# Revit family: EKF_EE_ПластронСВырезомTrivia_AVERES
name_source: partatom
category: Электрооборудование
units: mm (PartAtom-declared; Revit-internal decimal feet)

## family parameters
Всегда вертикально = Нет
На основе рабочей плоскости = Да
Общий = Да
При загрузке вырезать с полостями = Нет
Размер круглого соединителя = Использовать диаметр
Тип детали = Силовой щит
Точка расчета площади = Нет

## types (36) — shared parameters
ADSK_Единица измерения = шт.
ADSK_Завод-изготовитель = EKF
ADSK_Количество = 1
ADSK_Материал = RAL 7035_Сталь
Глубина = 400 мм
Изготовитель = EKF
Отметка по умолчанию = 1219.2 мм
Серия номенклатуры = Averes
Степень защиты IP = -
ТВ = EKF_2_TRIVIA_AVERES
Тип установки = -
Шаг_НабораПластронов_2шт = 100 мм
zero-valued in all types: ADSK_Масса

## per-type parameters (varying)
| type | ADSK_Код изделия | ADSK_Марка | ADSK_Наименование | ADSK_Обозначение | ADSK_Размер_Высота | ADSK_Размер_Глубина | ADSK_Размер_Ширина | Тип | Тип_Пластрона |
| Пластрон в вырезом  для горизонтального  ВА-99/160 3Р | FPFU2204 | Пластрон в вырезом для горизонтального ВА-99/160 3Р | Пластрон в вырезом для горизонтального ВА-99/160 3Р | Пластрон в вырезом для горизонтального ВА-99/160 3Р | 198 мм | 14 мм | 490 мм | 564 мм | Вл_Пластрон1 |
| Пластрон с вырезом  для горизонтального  AV POWER-1  ТМ 3P/4P с моторным приводом | FPFU1104 | Пластрон с вырезом для горизонтального AV POWER-1 ТМ 3P/4P с моторным приводом | Пластрон с вырезом для горизонтального AV POWER-1 ТМ 3P/4P с моторным приводом | Пластрон с вырезом для горизонтального AV POWER-1 ТМ 3P/4P с моторным приводом | 148 мм | 15 мм | 490 мм | 608 мм | Вл_Пластрон4 |
| Пластрон с вырезом для 1-го вертикального AV POWER-4 TM/ETU 3P EKF AVERES | FPFU1004 | Пластрон с вырезом для 1-го вертикального AV POWER-4 TM/ETU 3P EKF AVERES | Пластрон с вырезом для 1-го вертикального AV POWER-4 TM/ETU 3P EKF AVERES | Пластрон с вырезом для 1-го вертикального AV POWER-4 TM/ETU 3P EKF AVERES | 398 мм | 15 мм | 490 мм | 609 мм | Вл_Пластрон4 |
| Пластрон с вырезом для 3-х вертикальных AV POWER-3 TM/ETU 3P EKF AVERES | FPFU0904 | Пластрон с вырезом для 3-х вертикальных AV POWER-3 TM/ETU 3P EKF AVERES | Пластрон с вырезом для 3-х вертикальных AV POWER-3 TM/ETU 3P EKF AVERES | Пластрон с вырезом для 3-х вертикальных AV POWER-3 TM/ETU 3P EKF AVERES | 378 мм | 15 мм | 490 мм | 610 мм | Вл_Пластрон4 |
| Пластрон с вырезом для 4-х вертикальных AV POWER-1 ETU 3P EKF AVERES | FPFU0704 | Пластрон с вырезом для 4-х вертикальных AV POWER-1 ETU 3P EKF AVERES | Пластрон с вырезом для 4-х вертикальных AV POWER-1 ETU 3P EKF AVERES | Пластрон с вырезом для 4-х вертикальных AV POWER-1 ETU 3P EKF AVERES | 248 мм | 15 мм | 490 мм | 611 мм | Вл_Пластрон4 |
| Пластрон с вырезом для 4-х вертикальных AV POWER-1 TM 3P EKF AVERES | FPFU0604 | Пластрон с вырезом для 4-х вертикальных AV POWER-1 TM 3P EKF AVERES | Пластрон с вырезом для 4-х вертикальных AV POWER-1 TM 3P EKF AVERES | Пластрон с вырезом для 4-х вертикальных AV POWER-1 TM 3P EKF AVERES | 198 мм | 15 мм | 490 мм | 612 мм | Вл_Пластрон4 |
| Пластрон с вырезом для 4-х вертикальных AV POWER-2 TM/ETU 3P EKF AVERES | FPFU0804 | Пластрон с вырезом для 4-х вертикальных AV POWER-2 TM/ETU 3P EKF AVERES | Пластрон с вырезом для 4-х вертикальных AV POWER-2 TM/ETU 3P EKF AVERES | Пластрон с вырезом для 4-х вертикальных AV POWER-2 TM/ETU 3P EKF AVERES | 248 мм | 15 мм | 490 мм | 613 мм | Вл_Пластрон4 |
| Пластрон с вырезом для вертикальных ВА-99/125 4х3Р/3х4Р EKF AVERES | FPFU3104 | Пластрон с вырезом для вертикальных ВА-99/125 4х3Р/3х4Р EKF AVERES | Пластрон с вырезом для вертикальных ВА-99/125 4х3Р/3х4Р EKF AVERES | Пластрон с вырезом для вертикальных ВА-99/125 4х3Р/3х4Р EKF AVERES | 248 мм | 15 мм | 490 мм | 615 мм | Вл_Пластрон4 |
| Пластрон с вырезом для вертикальных ВА-99/250 3х3Р/3х4Р EKF AVERES | FPFU3304 | Пластрон с вырезом для вертикальных ВА-99/250 3х3Р/3х4Р EKF AVERES | Пластрон с вырезом для вертикальных ВА-99/250 3х3Р/3х4Р EKF AVERES | Пластрон с вырезом для вертикальных ВА-99/250 3х3Р/3х4Р EKF AVERES | 248 мм | 15 мм | 490 мм | 616 мм | Вл_Пластрон4 |
| Пластрон с вырезом для вертикальных ВА-99/400 3х3Р/2х4Р EKF AVERES | FPFU3404 | Пластрон с вырезом для вертикальных ВА-99/400 3х3Р/2х4Р EKF AVERES | Пластрон с вырезом для вертикальных ВА-99/400 3х3Р/2х4Р EKF AVERES | Пластрон с вырезом для вертикальных ВА-99/400 3х3Р/2х4Р EKF AVERES | 348 мм | 15 мм | 490 мм | 617 мм | Вл_Пластрон4 |
| Пластрон с вырезом для вертикальных ВА-99С/100/160/250 3х3Р EKF AVERES | FPFU6604 | Пластрон с вырезом для вертикальных ВА-99С/100/160/250 3х3Р EKF AVERES | Пластрон с вырезом для вертикальных ВА-99С/100/160/250 3х3Р EKF AVERES | Пластрон с вырезом для вертикальных ВА-99С/100/160/250 3х3Р EKF AVERES | 248 мм | 15 мм | 490 мм | 618 мм | Вл_Пластрон4 |
| Пластрон с вырезом для вертикальных ВА-99С/400/630 3х3Р/2х4Р EKF AVERES | FPFU6704 | Пластрон с вырезом для вертикальных ВА-99С/400/630 3х3Р/2х4Р EKF AVERES | Пластрон с вырезом для вертикальных ВА-99С/400/630 3х3Р/2х4Р EKF AVERES | Пластрон с вырезом для вертикальных ВА-99С/400/630 3х3Р/2х4Р EKF AVERES | 348 мм | 15 мм | 490 мм | 619 мм | Вл_Пластрон4 |
| Пластрон с вырезом для выкатного ВА-45/2000 3Р/4Р EKF AVERES | FPFU4404 | Пластрон с вырезом для выкатного ВА-45/2000 3Р/4Р EKF AVERES | Пластрон с вырезом для выкатного ВА-45/2000 3Р/4Р EKF AVERES | Пластрон с вырезом для выкатного ВА-45/2000 3Р/4Р EKF AVERES | 548 мм | 15 мм | 490 мм | 620 мм | Вл_Пластрон4 |
| Пластрон с вырезом для выкатного ВА-45/3200 3Р/4Р EKF AVERES | FPFU4504 | Пластрон с вырезом для выкатного ВА-45/3200 3Р/4Р EKF AVERES | Пластрон с вырезом для выкатного ВА-45/3200 3Р/4Р EKF AVERES | Пластрон с вырезом для выкатного ВА-45/3200 3Р/4Р EKF AVERES | 548 мм | 15 мм | 490 мм | 621 мм | Вл_Пластрон4 |
| Пластрон с вырезом для выкатного ВА-45/4000 3Р/4Р EKF AVERES | FPFU4604 | Пластрон с вырезом для выкатного ВА-45/4000 3Р/4Р EKF AVERES | Пластрон с вырезом для выкатного ВА-45/4000 3Р/4Р EKF AVERES | Пластрон с вырезом для выкатного ВА-45/4000 3Р/4Р EKF AVERES | 548 мм | 15 мм | 490 мм | 622 мм | Вл_Пластрон4 |
| Пластрон с вырезом для выкатного ВА-450 3Р/4Р EKF AVERES | FPFU4804 | Пластрон с вырезом для выкатного ВА-450 3Р/4Р EKF AVERES | Пластрон с вырезом для выкатного ВА-450 3Р/4Р EKF AVERES | Пластрон с вырезом для выкатного ВА-450 3Р/4Р EKF AVERES | 498 мм | 15 мм | 690 мм | 623 мм | Вл_Пластрон4 |
| Пластрон с вырезом для горизонтального AV POWER-1 ETU 3P EKF AVERES | FPFU0204 | Пластрон с вырезом для горизонтального AV POWER-1 ETU 3P EKF AVERES | Пластрон с вырезом для горизонтального AV POWER-1 ETU 3P EKF AVERES | Пластрон с вырезом для горизонтального AV POWER-1 ETU 3P EKF AVERES | 198 мм | 15 мм | 490 мм | 625 мм | Вл_Пластрон4 |
| Пластрон с вырезом для горизонтального AV POWER-1 TM 3P EKF AVERES | FPFU0104 | Пластрон с вырезом для горизонтального AV POWER-1 TM 3P EKF AVERES | Пластрон с вырезом для горизонтального AV POWER-1 TM 3P EKF AVERES | Пластрон с вырезом для горизонтального AV POWER-1 TM 3P EKF AVERES | 148 мм | 15 мм | 490 мм | 626 мм | Вл_Пластрон4 |
| Пластрон с вырезом для горизонтального AV POWER-2 TM/ETU 3P EKF AVERES | FPFU0304 | Пластрон с вырезом для горизонтального AV POWER-2 TM/ETU 3P EKF AVERES | Пластрон с вырезом для горизонтального AV POWER-2 TM/ETU 3P EKF AVERES | Пластрон с вырезом для горизонтального AV POWER-2 TM/ETU 3P EKF AVERES | 198 мм | 15 мм | 490 мм | 627 мм | Вл_Пластрон4 |
| Пластрон с вырезом для горизонтального AV POWER-3 TM/ETU 3P EKF AVERES | FPFU0404 | Пластрон с вырезом для горизонтального AV POWER-3 TM/ETU 3P EKF AVERES | Пластрон с вырезом для горизонтального AV POWER-3 TM/ETU 3P EKF AVERES | Пластрон с вырезом для горизонтального AV POWER-3 TM/ETU 3P EKF AVERES | 248 мм | 15 мм | 490 мм | 628 мм | Вл_Пластрон4 |
| Пластрон с вырезом для горизонтального AV POWER-4 TM/ETU 3P EKF AVERES | FPFU0504 | Пластрон с вырезом для горизонтального AV POWER-4 TM/ETU 3P EKF AVERES | Пластрон с вырезом для горизонтального AV POWER-4 TM/ETU 3P EKF AVERES | Пластрон с вырезом для горизонтального AV POWER-4 TM/ETU 3P EKF AVERES | 348 мм | 15 мм | 490 мм | 629 мм | Вл_Пластрон4 |
| Пластрон с вырезом для горизонтального ВА-99/125 3Р EKF AVERES | FPFU2104 | Пластрон с вырезом для горизонтального ВА-99/125 3Р EKF AVERES | Пластрон с вырезом для горизонтального ВА-99/125 3Р EKF AVERES | Пластрон с вырезом для горизонтального ВА-99/125 3Р EKF AVERES | 148 мм | 15 мм | 490 мм | 630 мм | Вл_Пластрон4 |
| Пластрон с вырезом для горизонтального ВА-99/250 3Р EKF AVERES | FPFU2304 | Пластрон с вырезом для горизонтального ВА-99/250 3Р EKF AVERES | Пластрон с вырезом для горизонтального ВА-99/250 3Р EKF AVERES | Пластрон с вырезом для горизонтального ВА-99/250 3Р EKF AVERES | 198 мм | 15 мм | 490 мм | 631 мм | Вл_Пластрон4 |
| Пластрон с вырезом для горизонтального ВА-99/400 3Р EKF AVERES | FPFU2404 | Пластрон с вырезом для горизонтального ВА-99/400 3Р EKF AVERES | Пластрон с вырезом для горизонтального ВА-99/400 3Р EKF AVERES | Пластрон с вырезом для горизонтального ВА-99/400 3Р EKF AVERES | 248 мм | 15 мм | 490 мм | 632 мм | Вл_Пластрон4 |
| Пластрон с вырезом для горизонтального ВА-99/800 3Р EKF AVERES | FPFU2504 | Пластрон с вырезом для горизонтального ВА-99/800 3Р EKF AVERES | Пластрон с вырезом для горизонтального ВА-99/800 3Р EKF AVERES | Пластрон с вырезом для горизонтального ВА-99/800 3Р EKF AVERES | 348 мм | 15 мм | 490 мм | 633 мм | Вл_Пластрон4 |
| Пластрон с вырезом для горизонтального ВА-99С/100/160/250 3Р/4Р | FPFU6204 | Пластрон с вырезом для горизонтального ВА-99С/100/160/250 3Р/4Р | Пластрон с вырезом для горизонтального ВА-99С/100/160/250 3Р/4Р | Пластрон с вырезом для горизонтального ВА-99С/100/160/250 3Р/4Р | 198 мм | 15 мм | 490 мм | 634 мм | Вл_Пластрон4 |
| Пластрон с вырезом для горизонтального ВА-99С/400/630 3Р/4Р EKF AVERES | FPFU6304 | Пластрон с вырезом для горизонтального ВА-99С/400/630 3Р/4Р EKF AVERES | Пластрон с вырезом для горизонтального ВА-99С/400/630 3Р/4Р EKF AVERES | Пластрон с вырезом для горизонтального ВА-99С/400/630 3Р/4Р EKF AVERES | 248 мм | 15 мм | 490 мм | 635 мм | Вл_Пластрон4 |
| Пластрон с вырезом для модульных устройств В200 мм EKF AVERES | FPFU5104 | Пластрон с вырезом для модульных устройств В200 мм EKF AVERES | Пластрон с вырезом для модульных устройств В200 мм EKF AVERES | Пластрон с вырезом для модульных устройств В200 мм EKF AVERES | 198 мм | 15 мм | 490 мм | 636 мм | Вл_Пластрон4 |
| Пластрон с вырезом для модульных устройств Ш800 В200 мм EKF AVERES | FPFU5804 | Пластрон с вырезом для модульных устройств Ш800 В200 мм EKF AVERES | Пластрон с вырезом для модульных устройств Ш800 В200 мм EKF AVERES | Пластрон с вырезом для модульных устройств Ш800 В200 мм EKF AVERES | 198 мм | 15 мм | 690 мм | 637 мм | Вл_Пластрон4 |
| Пластрон с вырезом для стационарного ВА-45/2000 3Р/4Р EKF AVERES | FPFU4204 | Пластрон с вырезом для стационарного ВА-45/2000 3Р/4Р EKF AVERES | Пластрон с вырезом для стационарного ВА-45/2000 3Р/4Р EKF AVERES | Пластрон с вырезом для стационарного ВА-45/2000 3Р/4Р EKF AVERES | 498 мм | 15 мм | 490 мм | 638 мм | Вл_Пластрон4 |
| Пластрон с вырезом для стационарного ВА-45/3200 3Р/4Р EKF AVERES | FPFU4304 | Пластрон с вырезом для стационарного ВА-45/3200 3Р/4Р EKF AVERES | Пластрон с вырезом для стационарного ВА-45/3200 3Р/4Р EKF AVERES | Пластрон с вырезом для стационарного ВА-45/3200 3Р/4Р EKF AVERES | 498 мм | 15 мм | 490 мм | 639 мм | Вл_Пластрон4 |
| Пластрон с вырезом для стационарного ВА-450 3Р/4Р EKF AVERES | FPFU4704 | Пластрон с вырезом для стационарного ВА-450 3Р/4Р EKF AVERES | Пластрон с вырезом для стационарного ВА-450 3Р/4Р EKF AVERES | Пластрон с вырезом для стационарного ВА-450 3Р/4Р EKF AVERES | 498 мм | 15 мм | 490 мм | 640 мм | Вл_Пластрон4 |
| Пластрон с вырезом для горизонтального AV POWER-2 TM/ETU 3/4P с мот.приводом EKF AVERES | FPFU1304 | Пластрон с вырезом для гор. AV POWER-2 TM/ETU 3/4P с мот.приводом EKF AVERES | Пластрон с вырезом для гор. AV POWER-2 TM/ETU 3/4P с мот.приводом EKF AVERES | Пластрон с вырезом для гор. AV POWER-2 TM/ETU 3/4P с мот.приводом EKF AVERES | 198 мм | 15 мм | 490 мм | 624 мм | Вл_Пластрон4 |
| Пластрон с вырезом для вертикального ВА-99/1600 3Р/4Р | FPFU6104 | Пластрон с вырезом для вертикального ВА-99/1600 3Р/4Р | Пластрон с вырезом для вертикального ВА-99/1600 3Р/4Р | Пластрон с вырезом для вертикального ВА-99/1600 3Р/4Р | 598 мм | 15 мм | 490 мм | 614 мм | Вл_Пластрон4 |
| Пластрон в вырезом  для вертикальных ВА-99/800 1х3Р/1х4Р | FPFU3504 | Пластрон в вырезом для вертикальных  ВА-99/800 1х3Р/1х4Р | Пластрон в вырезом для вертикальных  ВА-99/800 1х3Р/1х4Р | Пластрон в вырезом для вертикальных  ВА-99/800 1х3Р/1х4Р | 348 мм | 14 мм | 490 мм | 563 мм | Вл_Пластрон1 |
| Пластрон в вырезом  для вертикальных ВА-99/160 4х3Р/3х4Р | FPFU3204 | Пластрон в вырезом для вертикальных  ВА-99/160 4х3Р/3х4Р | Пластрон в вырезом для вертикальных  ВА-99/160 4х3Р/3х4Р | Пластрон в вырезом для вертикальных  ВА-99/160 4х3Р/3х4Р | 248 мм | 14 мм | 490 мм | 562 мм | Вл_Пластрон1 |
